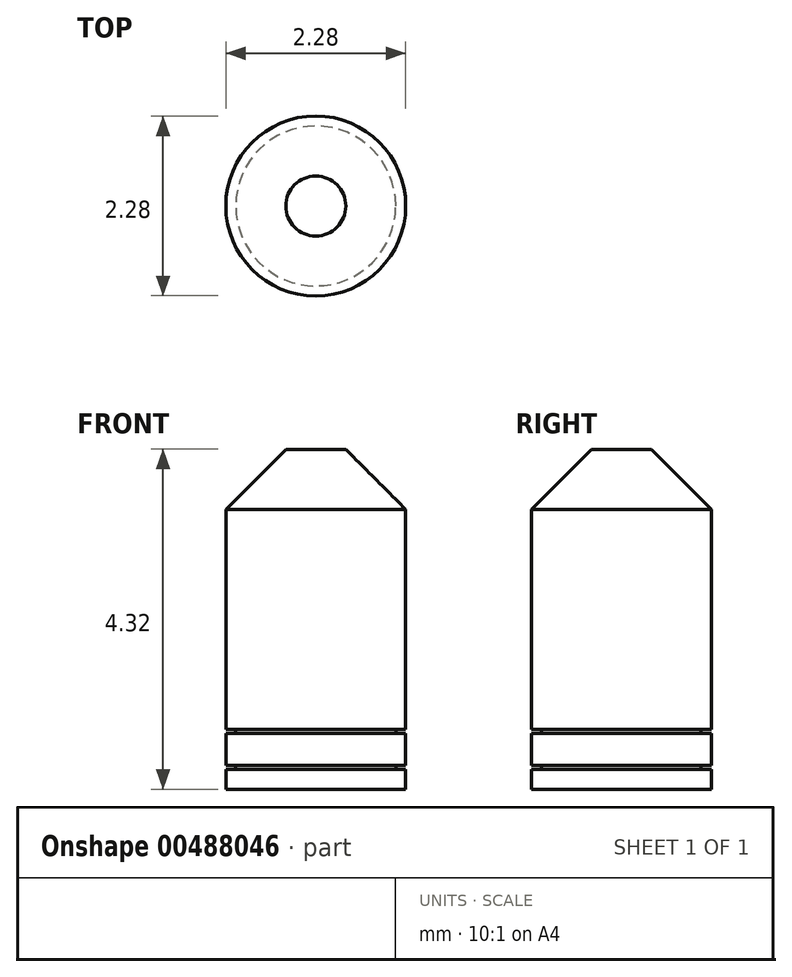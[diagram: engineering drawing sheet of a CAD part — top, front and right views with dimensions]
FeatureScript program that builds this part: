
annotation { "Feature Type Name" : "Feature", "Feature Type Description" : "" }
export const myFeature = defineFeature(function(context is Context, id is Id, definition is map)
    precondition{}
    {
        {
            var Q0;
            Q0=qCreatedBy(makeId("Top.planeOp"),FACE);
            var sketch = newSketch(context, id + "F0", { "sketchPlane" : qUnion([Q0])});
            skCircle(sketch, "E0", {"center": v(0, 0) * mm, "radius": 1.14 * mm});
            skSolve(sketch);
        }
        {
            var Q0;
            Q0=qSketchRegion(id+"F0",true);
            extrude(context, id + "F1", {"entities" : qUnion([Q0]), "depth" : 4.32 * mm, "offsetDistance" : 25.4 * mm});
        }
        {
            var Q0;
            Q0=qCreatedBy(makeId("Top.planeOp"),FACE);
            cPlane(context, id + "F2", {"entities" : qUnion([Q0]), "cplaneType" : CPlaneType.OFFSET, "offset" : 0.25 * mm, "width" : 152.4 * mm, "height" : 152.4 * mm});
        }
        {
            var Q0;
            Q0=qCreatedBy(id+"F2.planeOp",FACE);
            cPlane(context, id + "F3", {"entities" : qUnion([Q0]), "cplaneType" : CPlaneType.OFFSET, "offset" : 0.5 * mm, "width" : 152.4 * mm, "height" : 152.4 * mm});
        }
        {
            var Q0;
            Q0=qCreatedBy(id+"F2.planeOp",FACE);
            var sketch = newSketch(context, id + "F4", { "sketchPlane" : qUnion([Q0])});
            skCircle(sketch, "E1", {"center": v(0, 0) * mm, "radius": 1.02 * mm});
            skCircle(sketch, "E2", {"center": v(0, 0) * mm, "radius": 1.16 * mm});
            skSolve(sketch);
        }
        {
            var Q0;
            Q0=qSketchRegion(id+"F4",true);
            extrude(context, id + "F5", {"entities" : qUnion([Q0]), "operationType" : NewBodyOperationType.REMOVE, "depth" : 0.05 * mm, "offsetDistance" : 25.4 * mm});
        }
        {
            var Q0;
            Q0=qCreatedBy(id+"F3.planeOp",FACE);
            var sketch = newSketch(context, id + "F6", { "sketchPlane" : qUnion([Q0])});
            skCircle(sketch, "E3", {"center": v(0, 0) * mm, "radius": 1.16 * mm});
            skCircle(sketch, "E4", {"center": v(0, 0) * mm, "radius": 1.02 * mm});
            skSolve(sketch);
        }
        {
            var Q0;
            Q0=qSketchRegion(id+"F6",true);
            extrude(context, id + "F7", {"entities" : qUnion([Q0]), "operationType" : NewBodyOperationType.REMOVE, "oppositeDirection" : true, "depth" : 0.05 * mm, "offsetDistance" : 25.4 * mm});
        }
        {
            var Q0;
            Q0=makeQuery(id+"F1.opExtrude","CAP_EDGE",EDGE,{"disambiguationData":[OSD([sQuery(id+"F0.wireOp",EDGE,"E0")])],"isStart":false});
            chamfer(context, id + "F8", {"entities" : qUnion([Q0]), "width" : 0.76 * mm, "tangentPropagation" : true});
        }
    });
